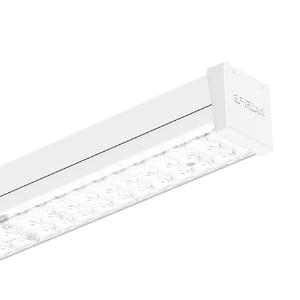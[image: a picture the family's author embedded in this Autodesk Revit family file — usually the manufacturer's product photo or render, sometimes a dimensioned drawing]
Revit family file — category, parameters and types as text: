
# Revit family: 3f_filippi_-_3f_linux_l_ugr_3f_filippi_-_a20668_-_3f_linux_l_40_led_dali_ugr_l1778__ip54__b957
name_source: partatom
category: Lighting Fixtures
units: mm (PartAtom-declared; Revit-internal decimal feet)

## family parameters
Cut with Voids When Loaded = No
Host = Face
Light Source = No
Part Type = Normal
Room Calculation Point = No
Round Connector Dimension = Use Diameter
Shared = No

## types (1)
- 3F Filippi - 3F Linux L UGR (1 x LED, 6664 lm, 40 W, 4000 K)
    Apparent Load = 40 VA
    Approval mark = CE
    CIE Flux Codes = 83 96 99 97 100
    Color Rendering = 80
    Color Temperature = 4000 K
    Control Gear = Electronic transformer
    Default Elevation = 1800 mm
    Description = Light unit for structure continues 3F Linux S.

ILLUMINOTECHNICAL
Luminous efficiency 100% (DLOR 97%, ULOR 3%).
Initial luminous flux of the luminaire 6664 lm.
Direct symmetric distribution.
Installation Interdistance Transv.D = 1.39 x hu - Long.D = 1.30 x hu.
Average luminance <3000 cd/m² for radial angles >65°.
Tabular UGR (CIE 117 - 4H-8H; S=0.25H; 70/50/20): RUG 18.4 - 16.7.
Beam angle: 78° - 75°.
Luminous efficacy 167 lm/W.
Lifetime (L93/B10): 30000 h. (tq+25°C)
Lifetime (L90/B10): 50000 h. (tq+25°C)
Lifetime (L85/B10): 80000 h. (tq+25°C)
Lifetime (L80/B10): 100000 h. (tq+25°C)
Lifetime (L85/B10): 50000 h. (tq+50°C)
Sudden decreased luminous flux after 50000 hours: 0% (C0).
Photobiological safety in compliance with IEC/TR 62778: RG0 risk exempt, (IEC 62471).
In compliance with IEC/EN 62722-2-1 - IEC/EN 62717 standards.

SOURCE
Linear LED module 40W/840.
Energy efficiency class (UE 2019/2020 - UE 2019/2015): C.
CIE 13.3 Colour rendering index: CRI >80 (R9 <50%).
IES TM-30 Fidelity Index: Rf = 84 Rg = 95.
CCT nominal colour temperature 4000 K.
Colour initial tolerance (MacAdam): SDCM 3.

MECHANICAL
Light unit in hot-galvanised steel, painted in white polyester base with fixing springs and retractable safety hooks in stainless steel.
Transparent methacrylate (PMMA) controlled distribution lenses with flat external surface.
Luminaire with limited surface temperature. - D - (EN 60598-2-24)
Dimensions: 1778x65 mm, height 71 mm. Weight 2.41 kg.
IP40 protection degree.
In combination with the appropriate accessories: IP54 protection degree.
Mechanical strength to impacts IK06 (1 joule).
Glow-wire test resistance 650°C.

ELECTRICAL
Halogen Free DALI-2, PUSH-DIM, electronic wiring 230V-50/60Hz, power factor 0.95 at full load, THD <25%, constant output current, class I, 1 driver, 1 DALI addresse.
Power of the luminaire 40 W.
ENEC - CE.
SAFE FLICKER: PstLM=<1 and SVM=<0.4 (IEC TR 61547-1 and IEC TR 63158), to ensure a more comfortable and safe light.
Luminaire compliant with EN 60598-2-22 for power supply from a centralised emergency system CPSS (Central Power Supply System), not incorporated in the luminaire - high risk areas excluded. The default power and flux are 100% in AC and 15% in DC.
Ambient temperature from 0°C to +45°C.
Temperature class T6 max 85°C.
Connection to the structure with 5-pin plug with phase selection (H05Z-U Halogen Free cable section 0.5 mm² HT90).
Relative humidity UR: <85%.

INSTALLATION
Ceiling / Suspended / Wall.
All accessories dedicated to this product are available on the Catalog and on our website www.3F-Filippi.com.

STRUCTURE
Hot-galvanised wired structure, painted in polyester base white, obtained through rolling process, with expanded EPDM rubber profiles.
Linear connecting element in hot galvanised steel with gasket for the formation of continuous channels, standard on L3556 versions (optional for other lengths).
Transparent polycarbonate IP54 cover element with methacrylate (PMMA) flexible parts.
The L3556 versions have a locking collar for joining the covers.
A20723 - 33F Linux system 7P IP54 L3556, structure with through-wiring 7-pole.
A20724 - 33F Linux system 7P IP54 L1778, structure with through-wiring 7-pole.
A20725 - 33F Linux system 5P IP54 L3556, structure with through-wiring 5-pole.
A20726 - 33F Linux system 5P IP54 L1778, structure with through-wiring 5-pole.

APPLICATIONS
Suitable product for food production plants (HACCP), IFS (Food Version 6), BRC (GSFS Food Version 7).
In commercial environments, exhibition areas, shops and stores.
In environments with VDTs, managerial offices and staterooms, public offices and schools.

LIGHT MANAGEMENT
Recommended minimum setting: 10%.
The device, equipped with DALI-2 driver, can be controlled manually with 3F Easy Dim technology or automatically/manually with 3F Smart Dimming technology and/or centralised DALI systems.
DALI-2 certification guarantees interoperability with other devices with the same certification.
In electrical systems without a regulation system (manual or automatic) and DALI bus, a suitable jumper must be made on the DA-DA terminals of the appliance.

WARNING
Luminaire designed for disposal/recycling at end-of-life.
Replaceable (LED only) light source by a professional. Replaceable control gear by a professional.
    Height = 71 mm
    Lamp = 1 x LED
    Lamp Light Flux = 6664 lm
    Lamp Power = 40 W
    Lamp count = 1
    Length = 1778 mm
    Lifetime = 50000 h
    Luminous efficacy = 167 lm/W
    Manufacturer = 3F Filippi
    ModVariant = No
    Model = 3F Filippi - A20668 - 3F Linux L 40 LED DALI UGR L1778 (IP54)
    Mounting Place = Ceiling
    Mounting Type = Pendant
    Number of Poles = 1
    OnlyDefault = Yes
    Power Factor = 1
    Product Name = 3F Filippi - 3F Linux L UGR
    Product group = pendant luminaire
    ProductGroupID = 9
    Protection Class = Protection class I
    Protection Degree = IP 54
    RLX_Detail_Level = 1
    RLX_Emergency_Light_Flux = 0 lm
    RLX_Emergency_Type = 0
    RLX_Emergency_Type_DB = No
    RlxData = <blob elided: 49381 chars, md5=6bdc16d6>
    Socket = socket
    Standby Power = 0 W
    System Light Flux = 6664 lm
    System Power = 40 W
    Type Comments = Product without accessories
    Type Image = 3ffilippi_3f_linux_l_ip54.jpg
    URL = http://relux.com
    VarID = ---
    Voltage = 0 V
    Weight = 0.00 kg
    Width = 65 mm

## geometry (parser evidence)
native form markers: Blend x4, Sweep x11
no freeform markers — native parametric forms only
